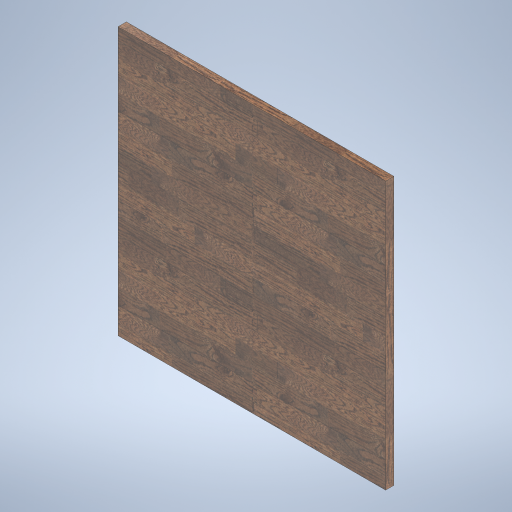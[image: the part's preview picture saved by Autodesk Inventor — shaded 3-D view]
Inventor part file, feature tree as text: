
AUTODESK INVENTOR PART (.ipt)
format: ipt  version: 2023 (Build 270158000, 158)  size: 387,584 bytes
history: native  units: mm
features: other x1, extrude x1, sketch x1
ambient origin geometry x8: Origin, YZ Plane, XZ Plane, XY Plane, X Axis, Y Axis, Z Axis, Center Point
bodies: Body1 (feature_tree)
feature tree (3):
  other  "솔리드1"
  extrude  "돌출1"  Depth=1000.0mm
  sketch  "스케치1"
